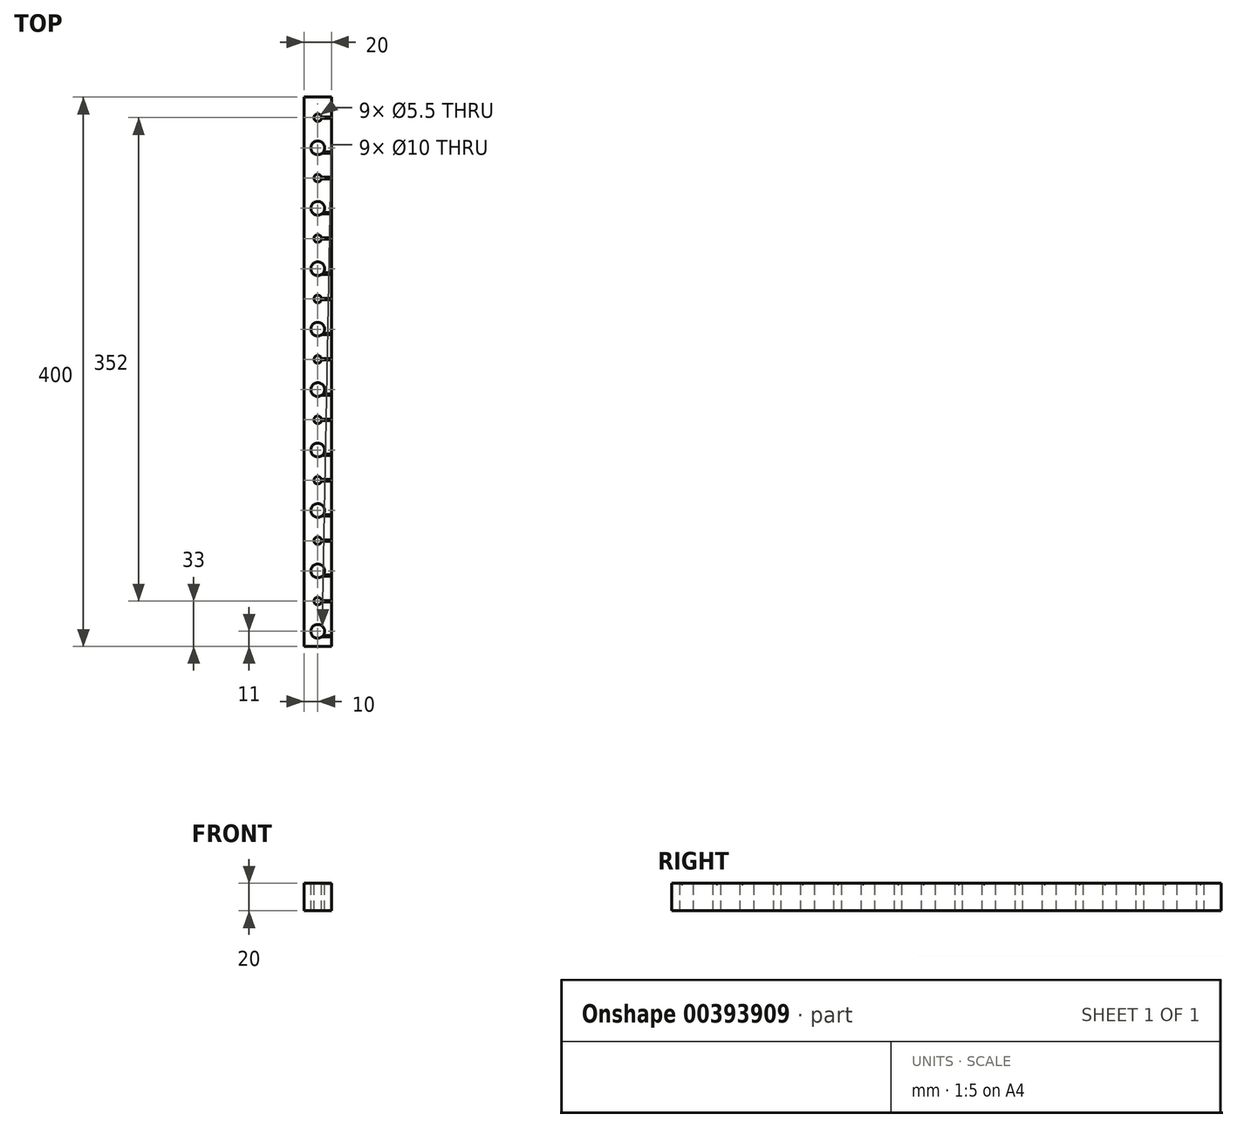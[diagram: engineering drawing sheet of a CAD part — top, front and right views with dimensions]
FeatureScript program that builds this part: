
annotation { "Feature Type Name" : "Feature", "Feature Type Description" : "" }
export const myFeature = defineFeature(function(context is Context, id is Id, definition is map)
    precondition{}
    {
        {
            var Q0;
            Q0=qCreatedBy(makeId("Right.planeOp"),FACE);
            var sketch = newSketch(context, id + "F0", { "sketchPlane" : qUnion([Q0])});
            skLineSegment(sketch, "E0.bottom", {"start": v(200, 10) * mm, "end": v(-200, 10) * mm});
            skLineSegment(sketch, "E0.top", {"start": v(200, -10) * mm, "end": v(-200, -10) * mm});
            skLineSegment(sketch, "E0.left", {"start": v(200, 10) * mm, "end": v(200, -10) * mm});
            skLineSegment(sketch, "E0.right", {"start": v(-200, 10) * mm, "end": v(-200, -10) * mm});
            skPoint(sketch, "E0.middle", {"position": v(0, 0) * mm});
            skSolve(sketch);
        }
        {
            var Q0;
            Q0=makeQuery(id+"F0.imprint","IMPRINT",FACE,{"disambiguationData":[TD([[makeQuery(id+"F0.imprint","IMPRINT",EDGE,{"derivedFrom":sQuery(id+"F0.wireOp",EDGE,"E0.bottom")}),1.0]])]});
            extrude(context, id + "F1", {"entities" : qUnion([Q0]), "depth" : 20 * mm});
        }
        {
            var Q0;
            Q0=makeQuery(id+"F1.opExtrude","SWEPT_FACE",FACE,{"disambiguationData":[OSD([sQuery(id+"F0.wireOp",EDGE,"E0.bottom")])]});
            var sketch = newSketch(context, id + "F2", { "sketchPlane" : qUnion([Q0])});
            skLineSegment(sketch, "E1", {"start": v(10, 200) * mm, "end": v(10, -200) * mm, "construction": true});
            skCircle(sketch, "E2", {"center": v(10, 185) * mm, "radius": 3 * mm});
            skCircle(sketch, "E3", {"center": v(10, 141) * mm, "radius": 3 * mm});
            skCircle(sketch, "E4", {"center": v(10, 97) * mm, "radius": 3 * mm});
            skCircle(sketch, "E5", {"center": v(10, 53) * mm, "radius": 3 * mm});
            skCircle(sketch, "E6", {"center": v(10, 9) * mm, "radius": 3 * mm});
            skCircle(sketch, "E7", {"center": v(10, -35) * mm, "radius": 3 * mm});
            skCircle(sketch, "E8", {"center": v(10, -79) * mm, "radius": 3 * mm});
            skCircle(sketch, "E9", {"center": v(10, -123) * mm, "radius": 3 * mm});
            skCircle(sketch, "E10", {"center": v(10, -167) * mm, "radius": 3 * mm});
            skSolve(sketch);
        }
        {
            var Q0;
            Q0=sQuery(id+"F2.wireOp",VERTEX,"E2.center");
            var Q1;
            Q1=sQuery(id+"F2.wireOp",VERTEX,"E3.center");
            var Q2;
            Q2=sQuery(id+"F2.wireOp",VERTEX,"E4.center");
            var Q3;
            Q3=sQuery(id+"F2.wireOp",VERTEX,"E10.center");
            var Q4;
            Q4=sQuery(id+"F2.wireOp",VERTEX,"E9.center");
            var Q5;
            Q5=sQuery(id+"F2.wireOp",VERTEX,"E8.center");
            var Q6;
            Q6=sQuery(id+"F2.wireOp",VERTEX,"E7.center");
            var Q7;
            Q7=sQuery(id+"F2.wireOp",VERTEX,"E6.center");
            var Q8;
            Q8=sQuery(id+"F2.wireOp",VERTEX,"E5.center");
            var Q9;
            Q9=makeQuery(id+"F1.opExtrude","SWEPT_BODY",BODY,{"disambiguationData":[OSD([sQuery(id+"F0.wireOp",EDGE,"E0.bottom"),sQuery(id+"F0.wireOp",EDGE,"E0.top"),sQuery(id+"F0.wireOp",EDGE,"E0.left"),sQuery(id+"F0.wireOp",EDGE,"E0.right")])]});
            hole(context, id + "F3", {"style" : HoleStyle.SIMPLE, "endStyle" : HoleEndStyle.BLIND, "holeDiameter" : 5.5 * mm, "holeDepth" : 20 * mm, "tappedDepth" : 12 * mm, "tapClearance" : 3, "locations" : qUnion([Q0, Q1, Q2, Q3, Q4, Q5, Q6, Q7, Q8]), "scope" : qUnion([Q9])});
        }
        {
            var Q0;
            Q0=makeQuery(id+"F1.opExtrude","SWEPT_FACE",FACE,{"disambiguationData":[OSD([sQuery(id+"F0.wireOp",EDGE,"E0.bottom")])]});
            var sketch = newSketch(context, id + "F4", { "sketchPlane" : qUnion([Q0])});
            skCircle(sketch, "E11", {"center": v(10, 163) * mm, "radius": 5 * mm});
            skPoint(sketch, "E11.centerSnap0", {"position": v(10, 200) * mm});
            skCircle(sketch, "E12", {"center": v(10, 119) * mm, "radius": 5 * mm});
            skCircle(sketch, "E13", {"center": v(10, 75) * mm, "radius": 5 * mm});
            skCircle(sketch, "E14", {"center": v(10, 31) * mm, "radius": 5 * mm});
            skCircle(sketch, "E15", {"center": v(10, -13) * mm, "radius": 5 * mm});
            skCircle(sketch, "E16", {"center": v(10, -57) * mm, "radius": 5 * mm});
            skCircle(sketch, "E17", {"center": v(10, -101) * mm, "radius": 5 * mm});
            skCircle(sketch, "E18", {"center": v(10, -145) * mm, "radius": 5 * mm});
            skCircle(sketch, "E19", {"center": v(10, -189) * mm, "radius": 5 * mm});
            skSolve(sketch);
        }
        {
            var Q0;
            Q0=sQuery(id+"F4.wireOp",VERTEX,"E11.center");
            var Q1;
            Q1=sQuery(id+"F4.wireOp",VERTEX,"E12.center");
            var Q2;
            Q2=sQuery(id+"F4.wireOp",VERTEX,"E13.center");
            var Q3;
            Q3=sQuery(id+"F4.wireOp",VERTEX,"E19.center");
            var Q4;
            Q4=sQuery(id+"F4.wireOp",VERTEX,"E18.center");
            var Q5;
            Q5=sQuery(id+"F4.wireOp",VERTEX,"E17.center");
            var Q6;
            Q6=sQuery(id+"F4.wireOp",VERTEX,"E16.center");
            var Q7;
            Q7=sQuery(id+"F4.wireOp",VERTEX,"E15.center");
            var Q8;
            Q8=sQuery(id+"F4.wireOp",VERTEX,"E14.center");
            var Q9;
            Q9=makeQuery(id+"F1.opExtrude","SWEPT_BODY",BODY,{"disambiguationData":[OSD([sQuery(id+"F0.wireOp",EDGE,"E0.bottom"),sQuery(id+"F0.wireOp",EDGE,"E0.top"),sQuery(id+"F0.wireOp",EDGE,"E0.left"),sQuery(id+"F0.wireOp",EDGE,"E0.right")])]});
            hole(context, id + "F5", {"style" : HoleStyle.SIMPLE, "endStyle" : HoleEndStyle.BLIND, "holeDiameter" : 10 * mm, "holeDepth" : 20 * mm, "tappedDepth" : 12 * mm, "tapClearance" : 3, "locations" : qUnion([Q0, Q1, Q2, Q3, Q4, Q5, Q6, Q7, Q8]), "scope" : qUnion([Q9])});
        }
        {
            var Q0;
            Q0=makeQuery(id+"F1.opExtrude","CAP_FACE",FACE,{"disambiguationData":[OSD([sQuery(id+"F0.wireOp",EDGE,"E0.bottom"),sQuery(id+"F0.wireOp",EDGE,"E0.top"),sQuery(id+"F0.wireOp",EDGE,"E0.left"),sQuery(id+"F0.wireOp",EDGE,"E0.right")])],"isStart":false});
            var sketch = newSketch(context, id + "F6", { "sketchPlane" : qUnion([Q0])});
            skArc(sketch, "E20", {"start": v(184.5, 10) * mm, "mid": v(185, 9.5) * mm, "end": v(185.5, 10) * mm});
            skArc(sketch, "E21", {"start": v(159, 10) * mm, "mid": v(159.5, 9.5) * mm, "end": v(160, 10) * mm});
            skArc(sketch, "E22", {"start": v(140.5, 10) * mm, "mid": v(141, 9.5) * mm, "end": v(141.5, 10) * mm});
            skArc(sketch, "E23", {"start": v(115, 10) * mm, "mid": v(115.5, 9.5) * mm, "end": v(116, 10) * mm});
            skArc(sketch, "E24", {"start": v(96.5, 10) * mm, "mid": v(97, 9.5) * mm, "end": v(97.5, 10) * mm});
            skArc(sketch, "E25", {"start": v(71, 10) * mm, "mid": v(71.5, 9.5) * mm, "end": v(72, 10) * mm});
            skArc(sketch, "E26", {"start": v(52.5, 10) * mm, "mid": v(53, 9.5) * mm, "end": v(53.5, 10) * mm});
            skArc(sketch, "E27", {"start": v(27, 10) * mm, "mid": v(27.5, 9.5) * mm, "end": v(28, 10) * mm});
            skArc(sketch, "E28", {"start": v(8.5, 10) * mm, "mid": v(9, 9.5) * mm, "end": v(9.5, 10) * mm});
            skArc(sketch, "E29", {"start": v(-17, 10) * mm, "mid": v(-16.5, 9.5) * mm, "end": v(-16, 10) * mm});
            skArc(sketch, "E30", {"start": v(-35.5, 10) * mm, "mid": v(-35, 9.5) * mm, "end": v(-34.5, 10) * mm});
            skArc(sketch, "E31", {"start": v(-61, 10) * mm, "mid": v(-60.5, 9.5) * mm, "end": v(-60, 10) * mm});
            skArc(sketch, "E32", {"start": v(-79.5, 10) * mm, "mid": v(-79, 9.5) * mm, "end": v(-78.5, 10) * mm});
            skArc(sketch, "E33", {"start": v(-105, 10) * mm, "mid": v(-104.5, 9.5) * mm, "end": v(-104, 10) * mm});
            skArc(sketch, "E34", {"start": v(-123.5, 10) * mm, "mid": v(-123, 9.5) * mm, "end": v(-122.5, 10) * mm});
            skArc(sketch, "E35", {"start": v(-149, 10) * mm, "mid": v(-148.5, 9.5) * mm, "end": v(-148, 10) * mm});
            skArc(sketch, "E36", {"start": v(-167.5, 10) * mm, "mid": v(-167, 9.5) * mm, "end": v(-166.5, 10) * mm});
            skArc(sketch, "E37", {"start": v(-193, 10) * mm, "mid": v(-192.5, 9.5) * mm, "end": v(-192, 10) * mm});
            skSolve(sketch);
        }
        {
            var Q0;
            {var subQ0=sQuery(id+"F6.wireOp",EDGE,"E25");Q0=makeQuery(id+"F6.imprint","IMPRINT",FACE,{"disambiguationData":[TD([[makeQuery(id+"F6.imprint","IMPRINT",EDGE,{"derivedFrom":subQ0}),1.0]])]});}
            var Q1;
            {var subQ0=sQuery(id+"F6.wireOp",EDGE,"E24");Q1=makeQuery(id+"F6.imprint","IMPRINT",FACE,{"disambiguationData":[TD([[makeQuery(id+"F6.imprint","IMPRINT",EDGE,{"derivedFrom":subQ0}),1.0]])]});}
            var Q2;
            {var subQ0=sQuery(id+"F6.wireOp",EDGE,"E23");Q2=makeQuery(id+"F6.imprint","IMPRINT",FACE,{"disambiguationData":[TD([[makeQuery(id+"F6.imprint","IMPRINT",EDGE,{"derivedFrom":subQ0}),1.0]])]});}
            var Q3;
            {var subQ0=sQuery(id+"F6.wireOp",EDGE,"E22");Q3=makeQuery(id+"F6.imprint","IMPRINT",FACE,{"disambiguationData":[TD([[makeQuery(id+"F6.imprint","IMPRINT",EDGE,{"derivedFrom":subQ0}),1.0]])]});}
            var Q4;
            {var subQ0=sQuery(id+"F6.wireOp",EDGE,"E21");Q4=makeQuery(id+"F6.imprint","IMPRINT",FACE,{"disambiguationData":[TD([[makeQuery(id+"F6.imprint","IMPRINT",EDGE,{"derivedFrom":subQ0}),1.0]])]});}
            var Q5;
            {var subQ0=sQuery(id+"F6.wireOp",EDGE,"E20");Q5=makeQuery(id+"F6.imprint","IMPRINT",FACE,{"disambiguationData":[TD([[makeQuery(id+"F6.imprint","IMPRINT",EDGE,{"derivedFrom":subQ0}),1.0]])]});}
            var Q6;
            {var subQ0=sQuery(id+"F6.wireOp",EDGE,"E26");Q6=makeQuery(id+"F6.imprint","IMPRINT",FACE,{"disambiguationData":[TD([[makeQuery(id+"F6.imprint","IMPRINT",EDGE,{"derivedFrom":subQ0}),1.0]])]});}
            var Q7;
            {var subQ0=sQuery(id+"F6.wireOp",EDGE,"E27");Q7=makeQuery(id+"F6.imprint","IMPRINT",FACE,{"disambiguationData":[TD([[makeQuery(id+"F6.imprint","IMPRINT",EDGE,{"derivedFrom":subQ0}),1.0]])]});}
            var Q8;
            {var subQ0=sQuery(id+"F6.wireOp",EDGE,"E28");Q8=makeQuery(id+"F6.imprint","IMPRINT",FACE,{"disambiguationData":[TD([[makeQuery(id+"F6.imprint","IMPRINT",EDGE,{"derivedFrom":subQ0}),1.0]])]});}
            var Q9;
            {var subQ0=sQuery(id+"F6.wireOp",EDGE,"E29");Q9=makeQuery(id+"F6.imprint","IMPRINT",FACE,{"disambiguationData":[TD([[makeQuery(id+"F6.imprint","IMPRINT",EDGE,{"derivedFrom":subQ0}),1.0]])]});}
            var Q10;
            {var subQ0=sQuery(id+"F6.wireOp",EDGE,"E30");Q10=makeQuery(id+"F6.imprint","IMPRINT",FACE,{"disambiguationData":[TD([[makeQuery(id+"F6.imprint","IMPRINT",EDGE,{"derivedFrom":subQ0}),1.0]])]});}
            var Q11;
            {var subQ0=sQuery(id+"F6.wireOp",EDGE,"E31");Q11=makeQuery(id+"F6.imprint","IMPRINT",FACE,{"disambiguationData":[TD([[makeQuery(id+"F6.imprint","IMPRINT",EDGE,{"derivedFrom":subQ0}),1.0]])]});}
            var Q12;
            {var subQ0=sQuery(id+"F6.wireOp",EDGE,"E32");Q12=makeQuery(id+"F6.imprint","IMPRINT",FACE,{"disambiguationData":[TD([[makeQuery(id+"F6.imprint","IMPRINT",EDGE,{"derivedFrom":subQ0}),1.0]])]});}
            var Q13;
            {var subQ0=sQuery(id+"F6.wireOp",EDGE,"E33");Q13=makeQuery(id+"F6.imprint","IMPRINT",FACE,{"disambiguationData":[TD([[makeQuery(id+"F6.imprint","IMPRINT",EDGE,{"derivedFrom":subQ0}),1.0]])]});}
            var Q14;
            {var subQ0=sQuery(id+"F6.wireOp",EDGE,"E34");Q14=makeQuery(id+"F6.imprint","IMPRINT",FACE,{"disambiguationData":[TD([[makeQuery(id+"F6.imprint","IMPRINT",EDGE,{"derivedFrom":subQ0}),1.0]])]});}
            var Q15;
            {var subQ0=sQuery(id+"F6.wireOp",EDGE,"E35");Q15=makeQuery(id+"F6.imprint","IMPRINT",FACE,{"disambiguationData":[TD([[makeQuery(id+"F6.imprint","IMPRINT",EDGE,{"derivedFrom":subQ0}),1.0]])]});}
            var Q16;
            {var subQ0=sQuery(id+"F6.wireOp",EDGE,"E36");Q16=makeQuery(id+"F6.imprint","IMPRINT",FACE,{"disambiguationData":[TD([[makeQuery(id+"F6.imprint","IMPRINT",EDGE,{"derivedFrom":subQ0}),1.0]])]});}
            var Q17;
            {var subQ0=sQuery(id+"F6.wireOp",EDGE,"E37");Q17=makeQuery(id+"F6.imprint","IMPRINT",FACE,{"disambiguationData":[TD([[makeQuery(id+"F6.imprint","IMPRINT",EDGE,{"derivedFrom":subQ0}),1.0]])]});}
            var Q18;
            {var subQ0=sQuery(id+"F6.wireOp",EDGE,"SgohaGzv-O8EL-MdpT-1y51-OWu1naZJhTZw");Q18=makeQuery(id+"F6.imprint","IMPRINT",FACE,{"disambiguationData":[TD([[makeQuery(id+"F6.imprint","IMPRINT",EDGE,{"derivedFrom":subQ0}),1.0]])]});}
            extrude(context, id + "F7", {"entities" : qUnion([Q0, Q1, Q2, Q3, Q4, Q5, Q6, Q7, Q8, Q9, Q10, Q11, Q12, Q13, Q14, Q15, Q16, Q17, Q18]), "operationType" : NewBodyOperationType.REMOVE, "oppositeDirection" : true, "depth" : 10 * mm});
        }
    });
